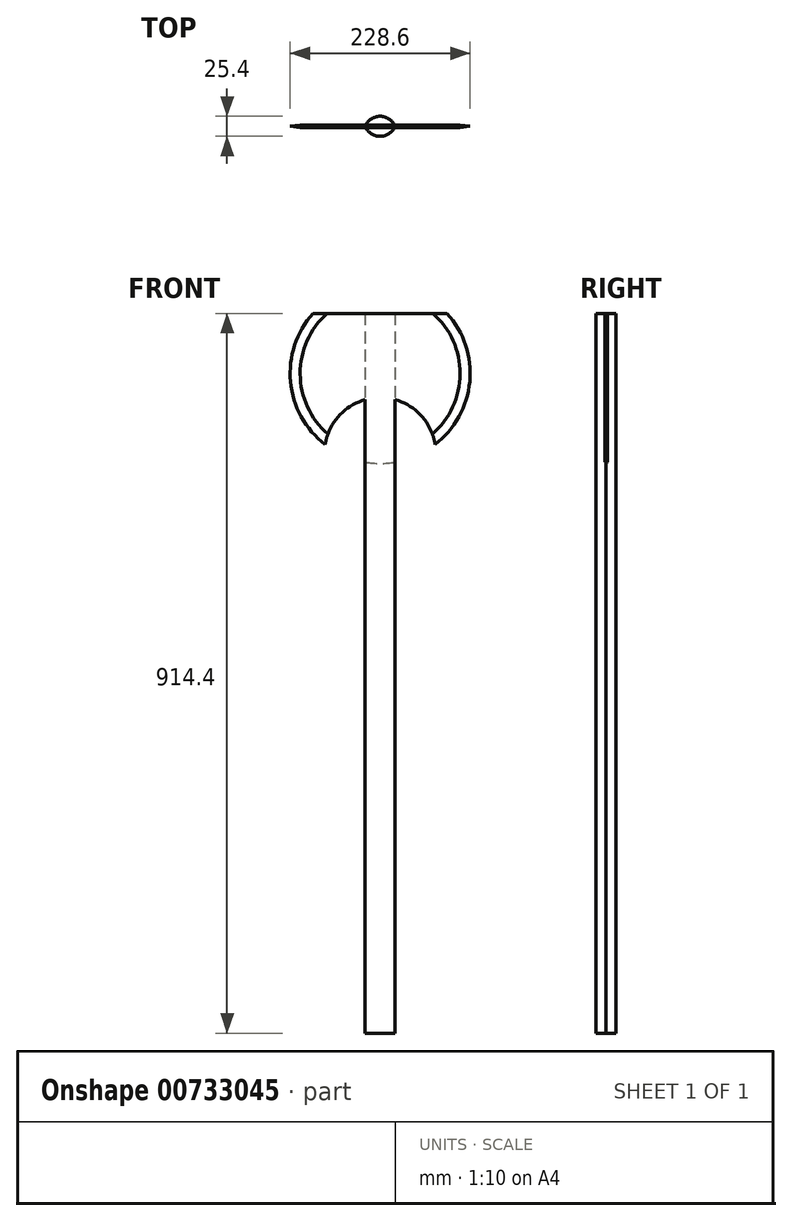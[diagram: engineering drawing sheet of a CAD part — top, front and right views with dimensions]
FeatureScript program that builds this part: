
annotation { "Feature Type Name" : "Feature", "Feature Type Description" : "" }
export const myFeature = defineFeature(function(context is Context, id is Id, definition is map)
    precondition{}
    {
        {
            var Q0;
            Q0=qCreatedBy(makeId("Top.planeOp"),FACE);
            var sketch = newSketch(context, id + "F0", { "sketchPlane" : qUnion([Q0])});
            skArc(sketch, "E0", {"start": v(19.05, 0) * mm, "mid": v(0, 12.7) * mm, "end": v(-19.05, 0) * mm});
            skArc(sketch, "E1", {"start": v(-19.05, 0) * mm, "mid": v(0, -12.7) * mm, "end": v(19.05, 0) * mm});
            skSolve(sketch);
        }
        {
            var Q0;
            Q0 = qSketchRegion(id + "F0", true);
            extrude(context, id + "F1", {"entities" : qUnion([Q0]), "depth" : 914.4 * mm, "offsetDistance" : 25.4 * mm});
        }
        {
            var Q0;
            Q0=qCreatedBy(makeId("Front.planeOp"),FACE);
            var sketch = newSketch(context, id + "F2", { "sketchPlane" : qUnion([Q0])});
            skArc(sketch, "E2", {"start": v(-85.2, 914.4) * mm, "mid": v(-113.82, 827.72) * mm, "end": v(-69.85, 747.73) * mm});
            skLineSegment(sketch, "E3", {"start": v(-85.2, 914.4) * mm, "end": v(85.2, 914.4) * mm});
            skArc(sketch, "E4", {"start": v(-69.85, 747.73) * mm, "mid": v(-52.8, 783.66) * mm, "end": v(-19.05, 804.72) * mm});
            skLineSegment(sketch, "E5", {"start": v(-19.05, 804.72) * mm, "end": v(-19.05, 725.5) * mm});
            skLineSegment(sketch, "E6", {"start": v(19.05, 804.72) * mm, "end": v(19.05, 725.5) * mm});
            skArc(sketch, "E7.trimOffspring", {"start": v(19.05, 804.72) * mm, "mid": v(52.8, 783.66) * mm, "end": v(69.85, 747.73) * mm});
            skArc(sketch, "E8.trimOffspring", {"start": v(69.85, 747.73) * mm, "mid": v(113.82, 827.72) * mm, "end": v(85.2, 914.4) * mm});
            skArc(sketch, "E9.trimOffspring", {"start": v(-19.05, 725.5) * mm, "mid": v(0, 723.9) * mm, "end": v(19.05, 725.5) * mm});
            skSolve(sketch);
        }
        {
            var Q0;
            Q0 = qSketchRegion(id + "F2", true);
            extrude(context, id + "F3", {"entities" : qUnion([Q0]), "depth" : 1.59 * mm, "offsetDistance" : 25.4 * mm, "hasSecondDirection" : true, "secondDirectionOppositeDirection" : true, "secondDirectionDepth" : 1.59 * mm});
        }
        {
            var Q0;
            Q0=makeQuery(id+"F3.opExtrude","CAP_EDGE",EDGE,{"disambiguationData":[OSD([sQuery(id+"F2.wireOp",EDGE,"E2")])],"isStart":false});
            var Q1;
            Q1=makeQuery(id+"F3.opExtrude","CAP_EDGE",EDGE,{"disambiguationData":[OSD([sQuery(id+"F2.wireOp",EDGE,"E8.trimOffspring")])],"isStart":false});
            chamfer(context, id + "F4", {"entities" : qUnion([Q0, Q1]), "chamferType" : ChamferType.TWO_OFFSETS, "width1" : 12.7 * mm, "oppositeDirection" : false, "width2" : 1.59 * mm, "tangentPropagation" : true});
        }
        {
            var Q0;
            Q0=makeQuery(id+"F3.opExtrude","CAP_EDGE",EDGE,{"disambiguationData":[OSD([sQuery(id+"F2.wireOp",EDGE,"E2")])],"isStart":true});
            var Q1;
            Q1=makeQuery(id+"F3.opExtrude","CAP_EDGE",EDGE,{"disambiguationData":[OSD([sQuery(id+"F2.wireOp",EDGE,"E8.trimOffspring")])],"isStart":true});
            chamfer(context, id + "F5", {"entities" : qUnion([Q0, Q1]), "chamferType" : ChamferType.TWO_OFFSETS, "width1" : 1.59 * mm, "oppositeDirection" : false, "width2" : 12.7 * mm, "tangentPropagation" : true});
        }
    });
